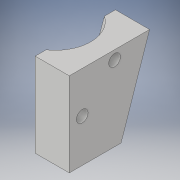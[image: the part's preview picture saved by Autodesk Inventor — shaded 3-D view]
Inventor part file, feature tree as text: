
AUTODESK INVENTOR PART (.ipt)
format: ipt  version: 2018 (Build 220112000, 112)  size: 184,832 bytes
history: native  units: in
note: dims shown in document units (in); Inventor stores cm internally (conversion verified against a paired STEP export)
features: sketch x8, extrude x4, loft x2, plane x1
ambient origin geometry x8: Origin, YZ Plane, XZ Plane, XY Plane, X Axis, Y Axis, Z Axis, Center Point
bodies: Solid1 (feature_tree)
feature tree (15):
  sketch  "Sketch1"  dims[d1=0.8in d2=1.2in]
  plane  "Work Plane1"
  loft  "Loft1"
  loft  "Loft2"
  extrude  "Extrusion1"  Depth=0.875in
  extrude  "Extrusion3"  TaperAngle=0.0deg  [1 undecoded]
  extrude  "Extrusion4"  Depth=1.6in
  extrude  "Extrusion5"  Depth=0.875in
  sketch  "Sketch3"  dims[d4=0.4in d5=2.8in]
  sketch  "Sketch4"  dims[d15=0.875in d17=0.875in]
  sketch  "Sketch5"  dims[d18=0.875in d19=0.0in d20=90.0deg]
  sketch  "Sketch6"  dims[d21=0.0in d22=90.0deg d23=1.6in]
  sketch  "Sketch8"  dims[d24=0.875in d26=0.875in]
  sketch  "Sketch9"  dims[d27=0.65in]
  sketch  "Sketch10"  dims[d28=0.0in d29=90.0deg d30=0.0in d31=90.0deg d32=0.4in d33=0.4in d34=0.4in d35=0.2in d36=0.0in d38=3.0in d39=0.0in d42=0.0in d43=0.25in d44=0.32in d45=0.09in d46=0.18in d47=0.2in d48=0.18in d49=0.5in d50=0.5in d51=1.0in d52=0.0in d53=1.5in d54=0.0in d55=1.5in d56=0.0in]
note: 1 required parameter value undecoded (feature->parameter linkage not recoverable at this tier; creation-order binding heuristic only, values carry confidence <= 0.55)
